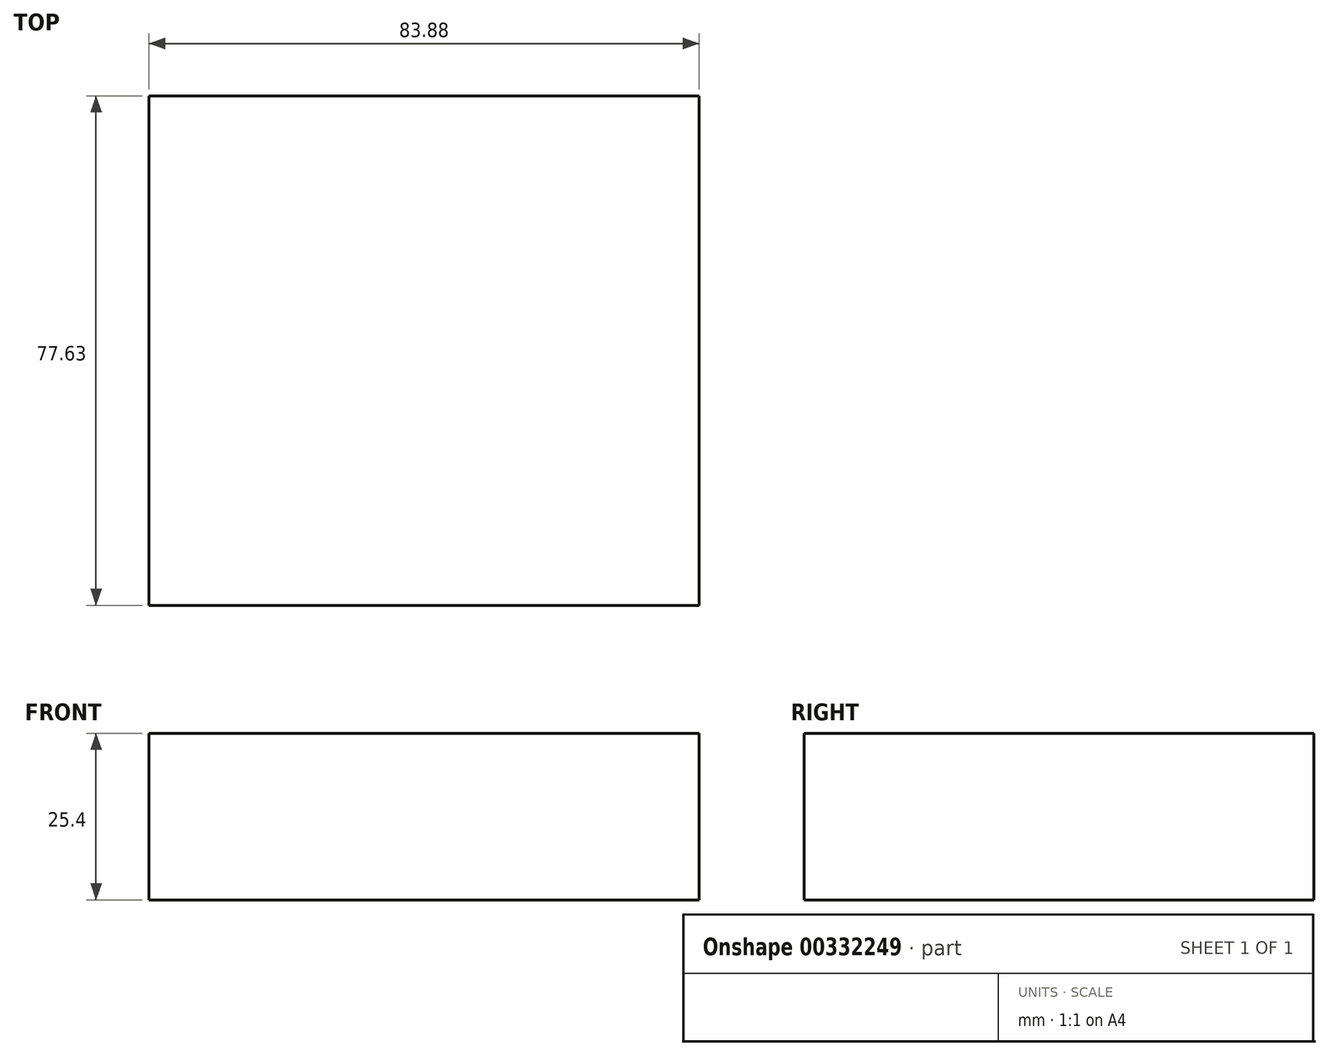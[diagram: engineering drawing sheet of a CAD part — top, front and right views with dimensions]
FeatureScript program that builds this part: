
annotation { "Feature Type Name" : "Feature", "Feature Type Description" : "" }
export const myFeature = defineFeature(function(context is Context, id is Id, definition is map)
    precondition{}
    {
        {
            var Q0;
            Q0=qCreatedBy(makeId("Top.planeOp"),FACE);
            var sketch = newSketch(context, id + "F0", { "sketchPlane" : qUnion([Q0])});
            skLineSegment(sketch, "E0.bottom", {"start": v(-40.09, 40.5) * mm, "end": v(43.79, 40.5) * mm});
            skLineSegment(sketch, "E0.top", {"start": v(-40.09, -37.13) * mm, "end": v(43.79, -37.13) * mm});
            skLineSegment(sketch, "E0.left", {"start": v(-40.09, 40.5) * mm, "end": v(-40.09, -37.13) * mm});
            skLineSegment(sketch, "E0.right", {"start": v(43.79, 40.5) * mm, "end": v(43.79, -37.13) * mm});
            skSolve(sketch);
        }
        {
            var Q0;
            Q0=makeQuery(id+"F0.imprint","IMPRINT",FACE,{"disambiguationData":[TD([[makeQuery(id+"F0.imprint","IMPRINT",EDGE,{"derivedFrom":sQuery(id+"F0.wireOp",EDGE,"E0.bottom")}),-1.0]])]});
            extrude(context, id + "F1", {"entities" : qUnion([Q0]), "endBound" : BoundingType.SYMMETRIC, "depth" : 25.4 * mm});
        }
    });
